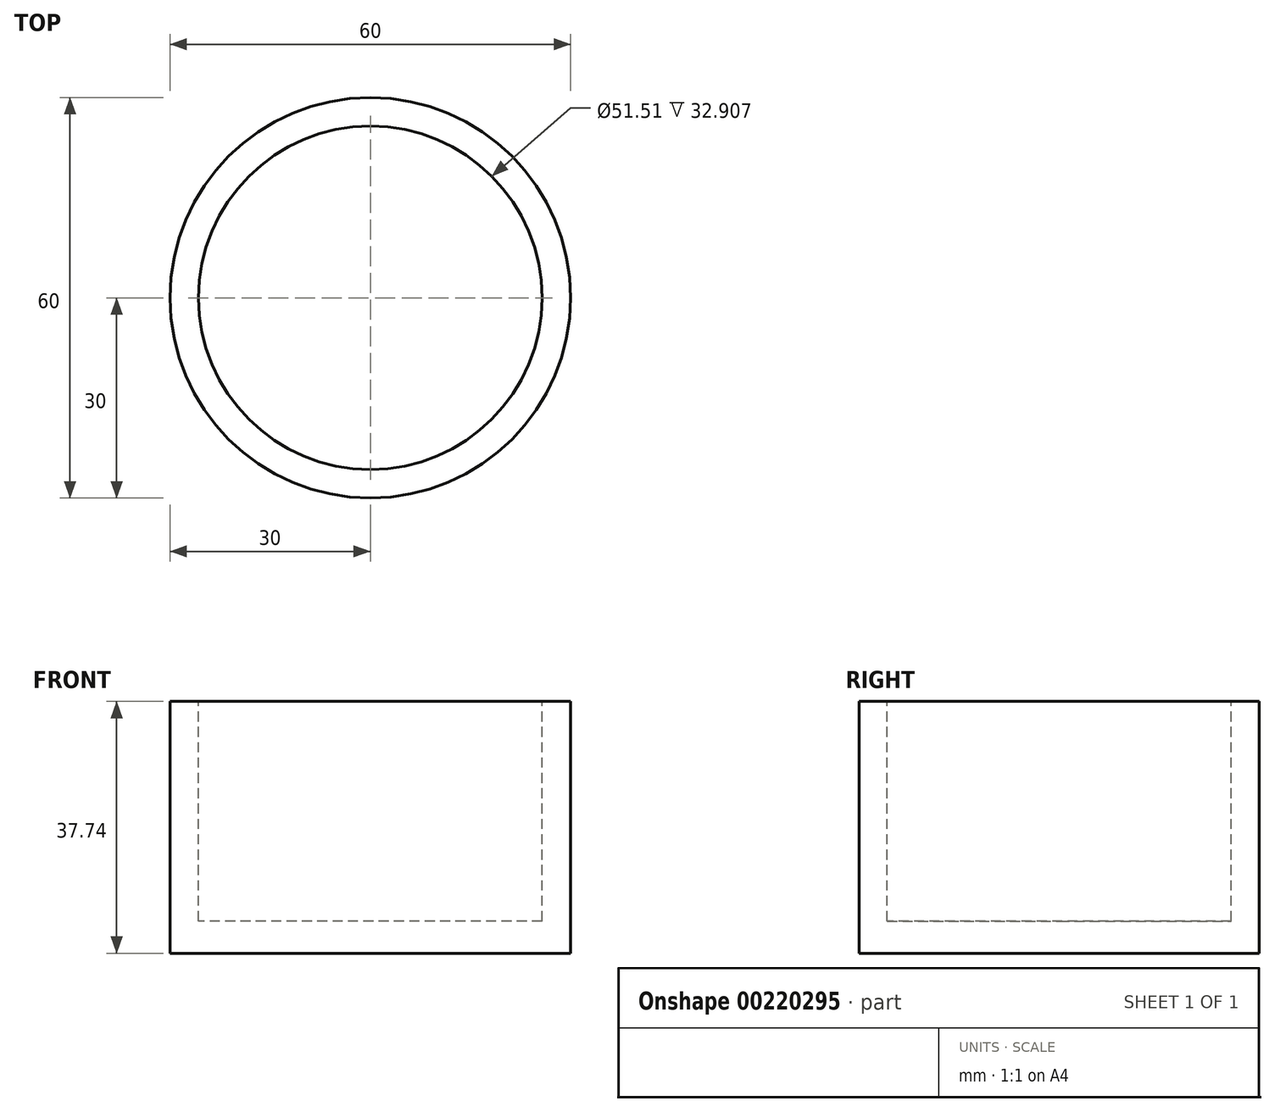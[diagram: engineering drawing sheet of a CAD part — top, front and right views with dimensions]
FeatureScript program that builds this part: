
annotation { "Feature Type Name" : "Feature", "Feature Type Description" : "" }
export const myFeature = defineFeature(function(context is Context, id is Id, definition is map)
    precondition{}
    {
        {
            var Q0;
            Q0=qCreatedBy(makeId("Front.planeOp"),FACE);
            var sketch = newSketch(context, id + "F0", { "sketchPlane" : qUnion([Q0])});
            skLineSegment(sketch, "E0", {"start": v(0, 0) * mm, "end": v(-30, 0) * mm});
            skLineSegment(sketch, "E1", {"start": v(-30, 0) * mm, "end": v(-30, 37.74) * mm});
            skLineSegment(sketch, "E2", {"start": v(-30, 37.74) * mm, "end": v(-25.75, 37.74) * mm});
            skLineSegment(sketch, "E3", {"start": v(-25.75, 37.74) * mm, "end": v(-25.75, 4.83) * mm});
            skLineSegment(sketch, "E4", {"start": v(-25.75, 4.83) * mm, "end": v(0, 4.83) * mm});
            skLineSegment(sketch, "E5", {"start": v(0, 4.83) * mm, "end": v(0, 0) * mm});
            skLineSegment(sketch, "E6", {"start": v(0, 69.21) * mm, "end": v(0, -56.7) * mm});
            skSolve(sketch);
        }
        {
            var Q0;
            Q0 = qSketchRegion(id + "F0", true);
            var Q1;
            Q1=sQuery(id+"F0.wireOp",EDGE,"E6");
            revolve(context, id + "F1", {"entities" : qUnion([Q0]), "axis" : qUnion([Q1]), "revolveType" : RevolveType.FULL});
        }
    });
